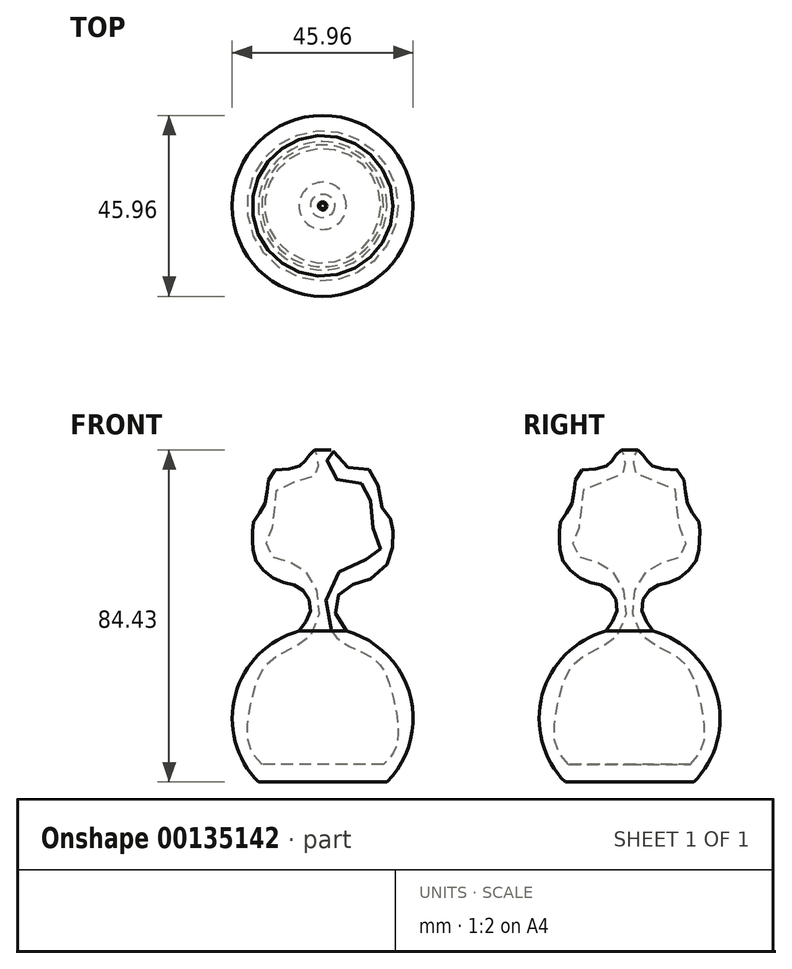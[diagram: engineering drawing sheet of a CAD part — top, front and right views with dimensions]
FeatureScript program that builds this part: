
annotation { "Feature Type Name" : "Feature", "Feature Type Description" : "" }
export const myFeature = defineFeature(function(context is Context, id is Id, definition is map)
    precondition{}
    {
        {
            var Q0;
            Q0=qCreatedBy(makeId("Front.planeOp"),FACE);
            var sketch = newSketch(context, id + "F0", { "sketchPlane" : qUnion([Q0])});
            skArc(sketch, "E0", {"start": v(-6, 22.18) * mm, "mid": v(-22.19, 5.97) * mm, "end": v(-16.32, -16.18) * mm});
            skFitSpline(sketch, "E1", {"points": [v(0, -16.18) * mm, v(-16.32, -16.18) * mm], "startDerivative": vector(-10.47, 0) * mm, "endDerivative": vector(-10.47, 0) * mm});
            skFitSpline(sketch, "E2", {"points": [v(-6, 22.18) * mm, v(-3.05, 28.28) * mm, v(-6, 33.33) * mm, v(-11.25, 35.01) * mm, v(-16.93, 40.06) * mm, v(-17.77, 45.1) * mm, v(-17.77, 49.1) * mm, v(-16.93, 51.2) * mm, v(-14.61, 54.78) * mm, v(-12.72, 62.77) * mm, v(-6, 64.03) * mm, v(-2, 68.23) * mm, v(-2, 61.72) * mm, v(-10.83, 59.2) * mm, v(-12.51, 49.52) * mm, v(-14.4, 42.16) * mm, v(-4.31, 37.32) * mm, v(-2.2, 22.18) * mm, v(-12.51, 15.46) * mm, v(-17.35, 7.46) * mm, v(-18.82, -6.62) * mm, v(-15.46, -11.67) * mm], "startDerivative": vector(98.2, 131.53) * mm, "endDerivative": vector(97.7, -93.63) * mm});
            skLineSegment(sketch, "E3", {"start": v(-15.46, -11.67) * mm, "end": v(0, -11.67) * mm});
            skLineSegment(sketch, "E4", {"start": v(0, -11.67) * mm, "end": v(0, -16.18) * mm});
            skLineSegment(sketch, "E5", {"start": v(0, 73.91) * mm, "end": v(0, -31.65) * mm});
            skSolve(sketch);
        }
        {
            var Q0;
            Q0=makeQuery(id+"F0.imprint","IMPRINT",FACE,{"disambiguationData":[TD([[makeQuery(id+"F0.imprint","IMPRINT",EDGE,{"derivedFrom":sQuery(id+"F0.wireOp",EDGE,"E0")}),1.0]])]});
            var Q1;
            Q1=sQuery(id+"F0.wireOp",EDGE,"E5");
            revolve(context, id + "F1", {"entities" : qUnion([Q0]), "axis" : qUnion([Q1]), "revolveType" : RevolveType.FULL});
        }
    });
